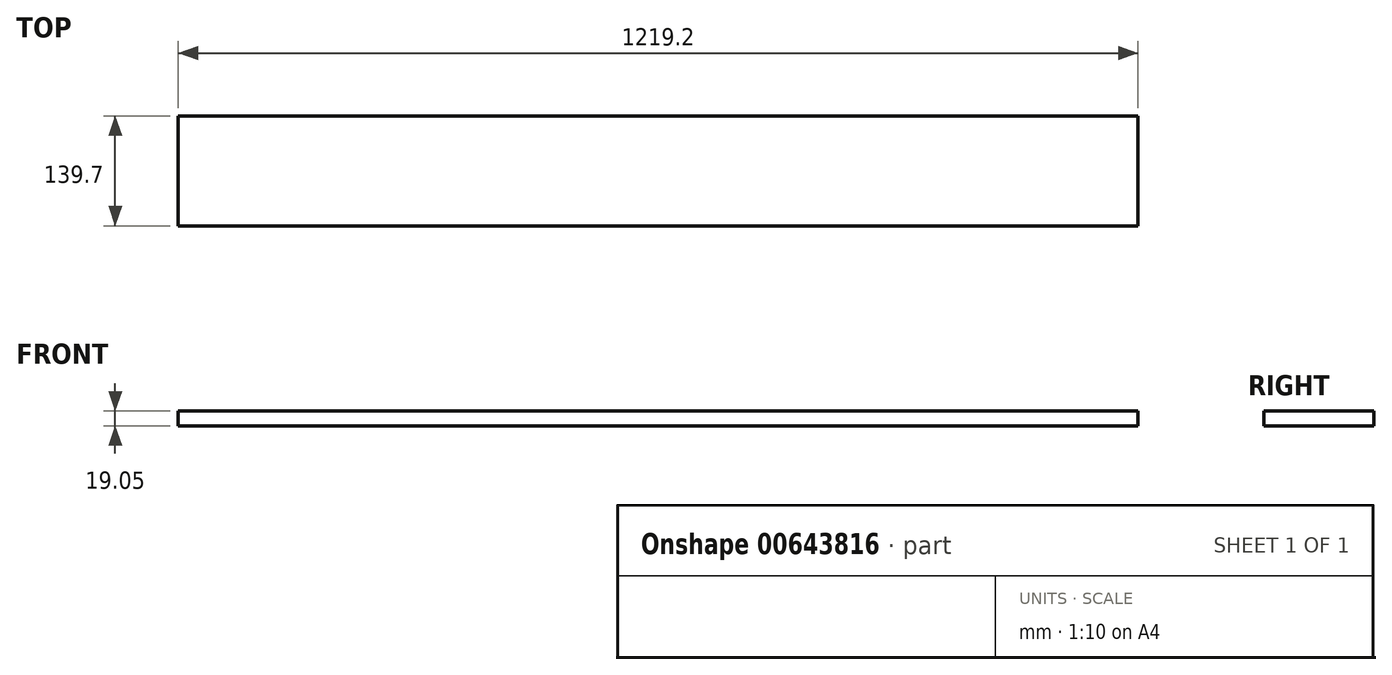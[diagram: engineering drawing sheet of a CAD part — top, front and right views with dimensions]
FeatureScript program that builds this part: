
annotation { "Feature Type Name" : "Feature", "Feature Type Description" : "" }
export const myFeature = defineFeature(function(context is Context, id is Id, definition is map)
    precondition{}
    {
        {
            var Q0;
            Q0=qCreatedBy(makeId("Top.planeOp"),FACE);
            var sketch = newSketch(context, id + "F0", { "sketchPlane" : qUnion([Q0])});
            skLineSegment(sketch, "E0.bottom", {"start": v(609.6, 69.85) * mm, "end": v(-609.6, 69.85) * mm});
            skLineSegment(sketch, "E0.top", {"start": v(609.6, -69.85) * mm, "end": v(-609.6, -69.85) * mm});
            skLineSegment(sketch, "E0.left", {"start": v(609.6, 69.85) * mm, "end": v(609.6, -69.85) * mm});
            skLineSegment(sketch, "E0.right", {"start": v(-609.6, 69.85) * mm, "end": v(-609.6, -69.85) * mm});
            skPoint(sketch, "E0.middle", {"position": v(0, 0) * mm});
            skSolve(sketch);
        }
        {
            var Q0;
            Q0 = qSketchRegion(id + "F0", true);
            extrude(context, id + "F1", {"entities" : qUnion([Q0]), "depth" : 19.05 * mm, "offsetDistance" : 25.4 * mm});
        }
    });
